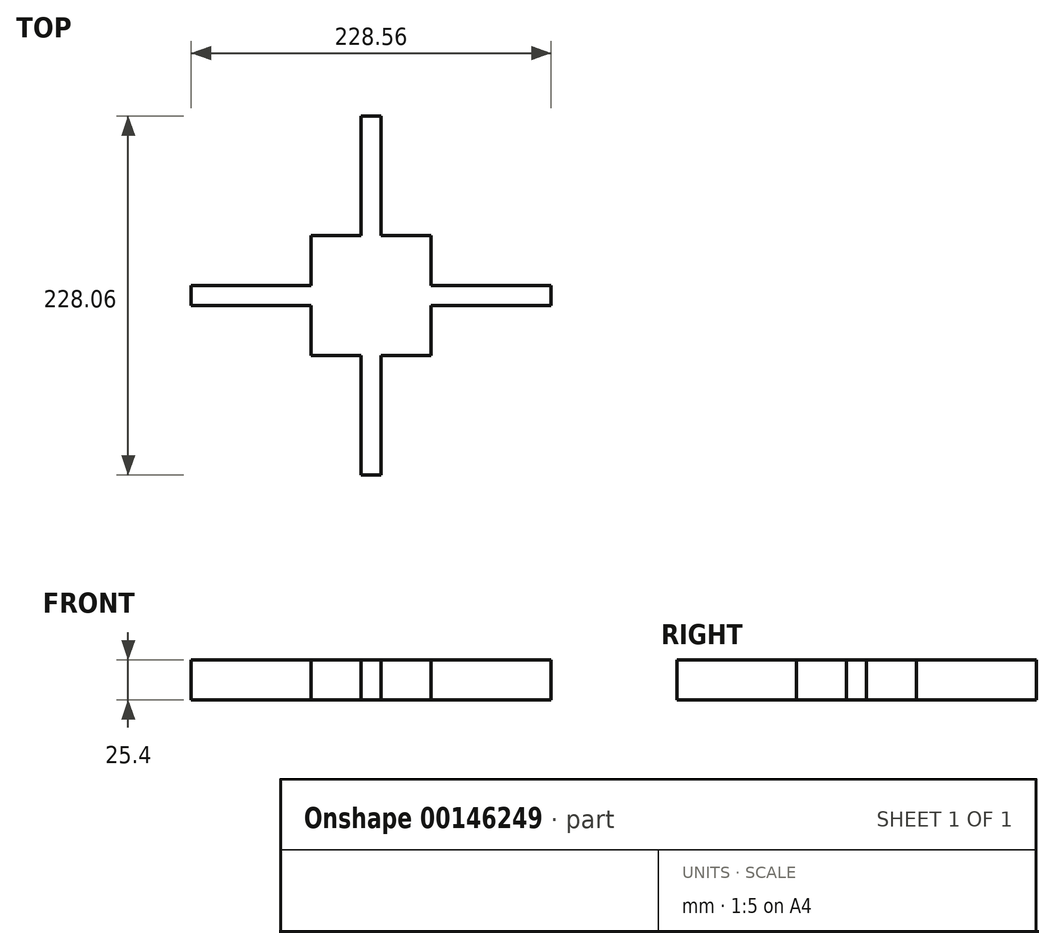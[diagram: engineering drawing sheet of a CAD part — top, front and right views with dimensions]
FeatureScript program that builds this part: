
annotation { "Feature Type Name" : "Feature", "Feature Type Description" : "" }
export const myFeature = defineFeature(function(context is Context, id is Id, definition is map)
    precondition{}
    {
        {
            var Q0;
            Q0=qCreatedBy(makeId("Top.planeOp"),FACE);
            var sketch = newSketch(context, id + "F0", { "sketchPlane" : qUnion([Q0])});
            skLineSegment(sketch, "E0.bottom", {"start": v(-37.89, 37.85) * mm, "end": v(38.31, 37.85) * mm});
            skLineSegment(sketch, "E0.top", {"start": v(-37.89, -38.35) * mm, "end": v(38.31, -38.35) * mm});
            skLineSegment(sketch, "E0.left", {"start": v(-37.89, 37.85) * mm, "end": v(-37.89, -38.35) * mm});
            skLineSegment(sketch, "E0.right", {"start": v(38.31, 37.85) * mm, "end": v(38.31, -38.35) * mm});
            skSolve(sketch);
        }
        {
            var Q0;
            Q0=makeQuery(id+"F0.imprint","IMPRINT",FACE,{"disambiguationData":[TD([[makeQuery(id+"F0.imprint","IMPRINT",EDGE,{"derivedFrom":sQuery(id+"F0.wireOp",EDGE,"E0.bottom")}),-1.0]])]});
            extrude(context, id + "F1", {"entities" : qUnion([Q0]), "depth" : 25.4 * mm});
        }
        {
            var Q0;
            Q0=qCreatedBy(makeId("Top.planeOp"),FACE);
            var sketch = newSketch(context, id + "F2", { "sketchPlane" : qUnion([Q0])});
            skLineSegment(sketch, "E1.bottom", {"start": v(-6.18, 37.67) * mm, "end": v(6.52, 37.67) * mm});
            skLineSegment(sketch, "E1.top", {"start": v(-6.18, 113.87) * mm, "end": v(6.52, 113.87) * mm});
            skLineSegment(sketch, "E1.left", {"start": v(-6.18, 37.67) * mm, "end": v(-6.18, 113.87) * mm});
            skLineSegment(sketch, "E1.right", {"start": v(6.52, 37.67) * mm, "end": v(6.52, 113.87) * mm});
            skSolve(sketch);
        }
        {
            var Q0;
            Q0=qCreatedBy(makeId("Top.planeOp"),FACE);
            var sketch = newSketch(context, id + "F3", { "sketchPlane" : qUnion([Q0])});
            skLineSegment(sketch, "E2.bottom", {"start": v(-6.26, -114.2) * mm, "end": v(6.44, -114.2) * mm});
            skLineSegment(sketch, "E2.top", {"start": v(-6.26, -38) * mm, "end": v(6.44, -38) * mm});
            skLineSegment(sketch, "E2.left", {"start": v(-6.26, -114.2) * mm, "end": v(-6.26, -38) * mm});
            skLineSegment(sketch, "E2.right", {"start": v(6.44, -114.2) * mm, "end": v(6.44, -38) * mm});
            skSolve(sketch);
        }
        {
            var Q0;
            Q0=qCreatedBy(makeId("Top.planeOp"),FACE);
            var sketch = newSketch(context, id + "F4", { "sketchPlane" : qUnion([Q0])});
            skLineSegment(sketch, "E3.bottom", {"start": v(-114.09, -6.54) * mm, "end": v(-37.89, -6.54) * mm});
            skLineSegment(sketch, "E3.top", {"start": v(-114.09, 6.16) * mm, "end": v(-37.89, 6.16) * mm});
            skLineSegment(sketch, "E3.left", {"start": v(-114.09, -6.54) * mm, "end": v(-114.09, 6.16) * mm});
            skLineSegment(sketch, "E3.right", {"start": v(-37.89, -6.54) * mm, "end": v(-37.89, 6.16) * mm});
            skSolve(sketch);
        }
        {
            var Q0;
            Q0=qCreatedBy(makeId("Top.planeOp"),FACE);
            var sketch = newSketch(context, id + "F5", { "sketchPlane" : qUnion([Q0])});
            skLineSegment(sketch, "E4.bottom", {"start": v(38.27, -6.56) * mm, "end": v(114.47, -6.56) * mm});
            skLineSegment(sketch, "E4.top", {"start": v(38.27, 6.14) * mm, "end": v(114.47, 6.14) * mm});
            skLineSegment(sketch, "E4.left", {"start": v(38.27, -6.56) * mm, "end": v(38.27, 6.14) * mm});
            skLineSegment(sketch, "E4.right", {"start": v(114.47, -6.56) * mm, "end": v(114.47, 6.14) * mm});
            skSolve(sketch);
        }
        {
            var Q0;
            Q0 = qSketchRegion(id + "F2", true);
            extrude(context, id + "F6", {"entities" : qUnion([Q0]), "operationType" : NewBodyOperationType.ADD, "depth" : 25.4 * mm});
        }
        {
            var Q0;
            Q0=makeQuery(id+"F4.imprint","IMPRINT",FACE,{"disambiguationData":[TD([[makeQuery(id+"F4.imprint","IMPRINT",EDGE,{"derivedFrom":sQuery(id+"F4.wireOp",EDGE,"E3.bottom")}),1.0]])]});
            extrude(context, id + "F7", {"entities" : qUnion([Q0]), "operationType" : NewBodyOperationType.ADD, "depth" : 25.4 * mm});
        }
        {
            var Q0;
            Q0=makeQuery(id+"F5.imprint","IMPRINT",FACE,{"disambiguationData":[TD([[makeQuery(id+"F5.imprint","IMPRINT",EDGE,{"derivedFrom":sQuery(id+"F5.wireOp",EDGE,"E4.bottom")}),1.0]])]});
            extrude(context, id + "F8", {"entities" : qUnion([Q0]), "operationType" : NewBodyOperationType.ADD, "depth" : 25.4 * mm});
        }
        {
            var Q0;
            Q0=makeQuery(id+"F3.imprint","IMPRINT",FACE,{"disambiguationData":[TD([[makeQuery(id+"F3.imprint","IMPRINT",EDGE,{"derivedFrom":sQuery(id+"F3.wireOp",EDGE,"E2.bottom")}),1.0]])]});
            extrude(context, id + "F9", {"entities" : qUnion([Q0]), "operationType" : NewBodyOperationType.ADD, "depth" : 25.4 * mm});
        }
    });
